# Revit family: SLSF2X2
name_source: partatom
category: Lighting Fixtures
units: mm (PartAtom-declared; Revit-internal decimal feet)

## family parameters
Always vertical = Yes
Cut with Voids When Loaded = No
Host = Ceiling
Light Source = Yes
Maintain Annotation Orientation = No
OmniClass Number = 23.80.70.11.14.17
OmniClass Title = Direct/Indirect
Part Type = Normal
Room Calculation Point = No
Round Connector Dimension = Use Diameter
Shared = No

## types (4) — shared parameters
Assembly Code = D5020200
Color Filter = 16777215
Default Elevation = 0' - 0"
Description = Architectural Suspended Luminaire  with Flat lens
Dimming Lamp Color Temperature Shift = <None>
Emit Shape Visible in Rendering = No
Emit from Rectangle Length = 1' - 10 1/2"
Emit from Rectangle Width = 1' - 10 1/2"
Housing Finish = Metal - Viscor - White
Lamp = LED
Length = 1' - 10 1/2"
Lens Finish = Acrylic - Viscor - Opal White Square
Manufacturer = VISIONEERING by VISCOR
Model = SLSF2X2
Tilt Angle = 90.00°
URL = https://viscor.com
Voltage = 120 V
Width = 1' - 10 1/2"

## per-type parameters (varying)
| type | Apparent Load | Emit from Rectangle Height | Lamp Wattage | Lens Depth | Photometric Web File |
| SLSF2X2-LED840K024LUNV | 18 VA | 0' - 4 3/32" | 18 VA | 0' - 4 3/32" | SLSF2X2-LED840K024LUNV.ies |
| SLSF2X2-LED840K034LUNV | 26 VA | 0' - 4 3/32" | 26 VA | 0' - 4 3/32" | SLSF2X2-LED840K034LUNV.ies |
| SLSF2X2-LED840K040LUNV | 32 VA | 0' - 4 3/32" | 32 VA | 0' - 4 3/32" | SLSF2X2-LED840K040LUNV.ies |
| SLSF2X2-LED840K050LUNV | 40 VA | 0' - 4 11/32" | 40 VA | 0' - 4 11/32" | SLSF2X2-LED840K050LUNV.ies |

## geometry (parser evidence)
native form markers: Sweep x3
no freeform markers — native parametric forms only
